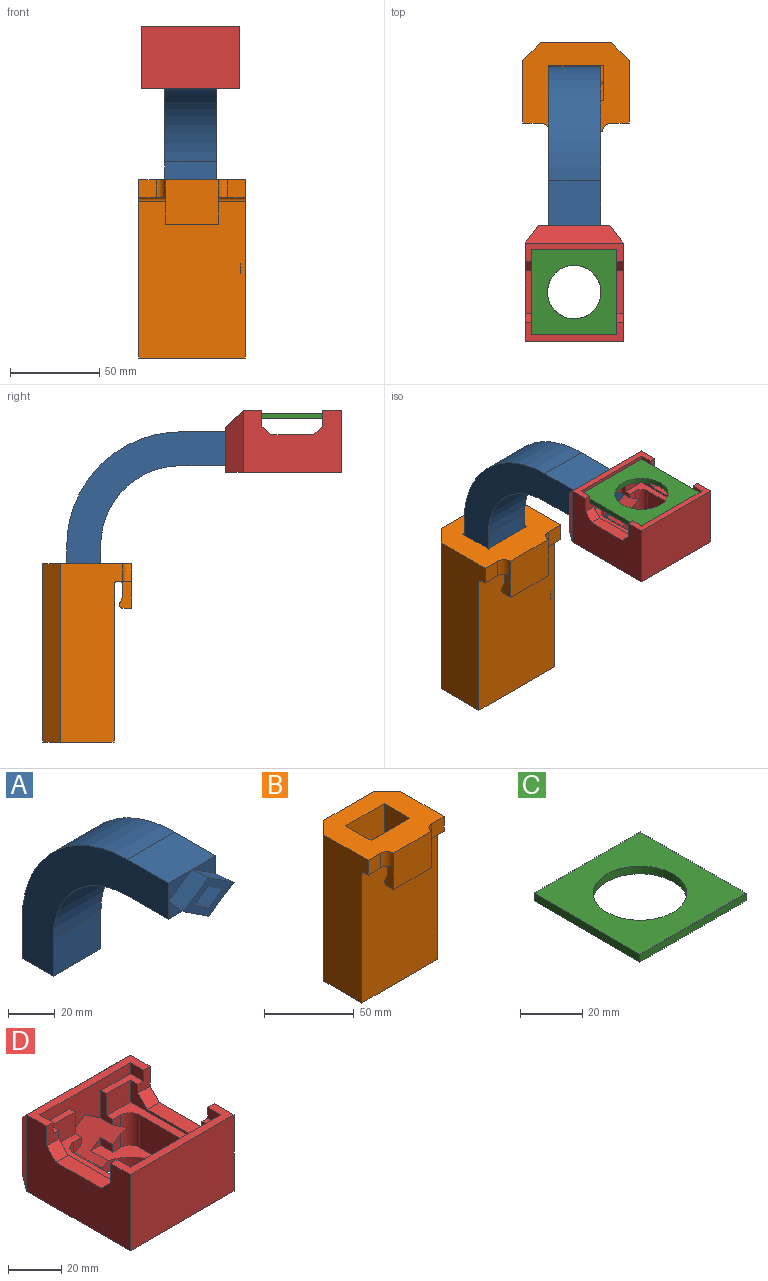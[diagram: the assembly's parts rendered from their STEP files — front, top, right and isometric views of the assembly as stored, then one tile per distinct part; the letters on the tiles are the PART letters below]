
ASSEMBLY  parts=4 mates=3
PART A: 34 faces, bbox 30.9x99x84.6 mm
  f0: plane 14.5x9.5mm, normal (0,-1,0), area 68.9mm2, adj f6,f11,f12
  f1: plane 14.5x9.5mm, normal (0,-1,0), area 68.9mm2, adj f5,f6,f19
  f2: plane 14.5x9.5mm, normal (0,-1,0), area 68.9mm2, adj f4,f5,f14
  f3: plane 14.5x9.5mm, normal (0,-1,0), area 68.9mm2, adj f4,f11,f13
  f4: plane 29x25mm, normal (0,0,-1), area 725mm2, adj f2,f3,f5,f11,f24
  f5: plane 89x84mm, normal (1,0,0), area 2481.6mm2, adj f1,f2,f4,f6,f24,f25,f30,f31
  f6: plane 29x25mm, normal (0,0,1), area 725mm2, adj f0,f1,f5,f11,f25
  f7: plane 25x9.24mm, normal (0.6,0,0.8), area 287.4mm2, adj f8,f10,f15,f22
  f8: plane 25x9.24mm, normal (0.6,0,-0.8), area 287.4mm2, adj f7,f9,f16,f21
  f9: plane 25x9.24mm, normal (-0.6,0,-0.8), area 287.4mm2, adj f8,f10,f17,f26
  f10: plane 25x9.24mm, normal (-0.6,0,0.8), area 287.4mm2, adj f7,f9,f18,f23
  f11: plane 89x84mm, normal (-1,0,0), area 2481.6mm2, adj f0,f3,f4,f6,f24,f25,f30,f31
  f12: plane 15.46x10.13mm, normal (-0.55,0.05,0.84), area 179.3mm2, adj f0,f13,f19,f20
  f13: plane 15.46x10.13mm, normal (-0.55,0.05,-0.84), area 179.3mm2, adj f3,f12,f14,f20
  f14: plane 15.46x10.13mm, normal (0.55,0.05,-0.84), area 179.3mm2, adj f2,f13,f19,f20
  f15: plane 10x9.24mm, normal (0.59,0.05,0.8), area 109.6mm2, adj f7,f16,f18,f20
  f16: plane 10x9.24mm, normal (0.59,0.05,-0.8), area 109.6mm2, adj f8,f15,f17,f20
  f17: plane 10x9.24mm, normal (-0.59,0.05,-0.8), area 109.6mm2, adj f9,f16,f18,f20
  f18: plane 10x9.24mm, normal (-0.59,0.05,0.8), area 109.6mm2, adj f10,f15,f17,f20
  f19: plane 15.46x10.13mm, normal (0.55,0.05,0.84), area 179.3mm2, adj f1,f12,f14,f20
  f20: plane 30.91x20.25mm, normal (0,-1,0), area 209.5mm2, adj f12,f13,f14,f15,f16,f17,f18,f19
  f21: cone r=61.35mm half-angle=36.6deg, axis (1,0,0), area 1046.1mm2, adj f8,f22,f26,f27
  f22: cone r=54.5mm half-angle=36.6deg, axis (-1,0,0), area 922.4mm2, adj f7,f21,f23,f28
  f23: cone r=47.65mm half-angle=36.6deg, axis (1,0,0), area 922.4mm2, adj f10,f22,f26,f29
  f24: cylinder r=45mm len=45mm, axis (1,0,0), area 2049.9mm2, adj f4,f5,f11,f30
  f25: cylinder r=64mm len=64mm, axis (1,0,0), area 2915.4mm2, adj f5,f6,f11,f31
  f26: cone r=54.5mm half-angle=36.6deg, axis (-1,0,0), area 1046.1mm2, adj f9,f21,f23,f32
  f27: plane 20x9.24mm, normal (0.6,-0.8,0), area 229.9mm2, adj f21,f28,f32,f33
  f28: plane 20x9.24mm, normal (0.6,0.8,0), area 229.9mm2, adj f22,f27,f29,f33
  f29: plane 20x9.24mm, normal (-0.6,0.8,0), area 229.9mm2, adj f23,f28,f32,f33
  f30: plane 29x20mm, normal (0,-1,0), area 580mm2, adj f5,f11,f24,f33
  f31: plane 29x20mm, normal (0,1,0), area 580mm2, adj f5,f11,f25,f33
  f32: plane 20x9.24mm, normal (-0.6,-0.8,0), area 229.9mm2, adj f26,f27,f29,f33
  f33: plane 29x19mm, normal (0,0,-1), area 424.5mm2, adj f5,f11,f27,f28,f29,f30,f31,f32
PART B: 74 faces, bbox 60x50x100 mm
  f0: plane 39.73x22.93mm, normal (-1,0,0), area 855.9mm2, adj f3,f4,f39,f41,f43,f47,f66
  f1: plane 100x35mm, normal (1,0,0), area 2326.3mm2, adj f4,f9,f15,f25,f26,f29,f32,f62
  f2: cylinder r=3.5mm len=7mm, axis (1,0,0), area 44mm2, adj f35,f63
  f3: plane 70x50mm, normal (0,1,0), area 2997.6mm2, adj f0,f4,f36,f40,f41,f42,f44,f45
  f4: plane 60x40mm, normal (0,0,-1), area 850mm2, adj f0,f1,f3,f13,f14,f15,f16,f25
  f5: plane 15.25x10mm, normal (0.55,0.84,0), area 182.4mm2, adj f6,f8,f19,f40
  f6: plane 15.25x10mm, normal (0.55,-0.84,0), area 182.4mm2, adj f5,f7,f24,f40
  f7: plane 15.25x10mm, normal (-0.55,-0.84,0), area 182.4mm2, adj f6,f8,f22,f40
  f8: plane 15.25x10mm, normal (-0.55,0.84,0), area 182.4mm2, adj f5,f7,f23,f40
  f9: plane 60x50mm, normal (0,0,1), area 2150.7mm2, adj f1,f11,f13,f14,f15,f16,f17,f18
  f10: plane 30x5mm, normal (0,0,-1), area 150mm2, adj f11,f28,f30,f54
  f11: plane 30x25mm, normal (0,-1,0), area 750mm2, adj f9,f10,f28,f30,f33,f34
  f12: plane 30x5.71mm, normal (0,1,0), area 171.3mm2, adj f28,f30,f31,f55
  f13: plane 100x35mm, normal (-1,0,0), area 3050.9mm2, adj f4,f9,f16,f25,f26,f27,f32
  f14: plane 100x40mm, normal (0,1,0), area 4000mm2, adj f4,f9,f15,f16
  f15: plane 100x10mm, normal (0.71,0.71,0), area 1407mm2, adj f1,f4,f9,f14,f62
  f16: plane 100x10mm, normal (-0.71,0.71,0), area 1414.2mm2, adj f4,f9,f13,f14
  f17: plane 20x20mm, normal (1,0,0), area 400mm2, adj f9,f18,f19,f21,f24
  f18: plane 30.5x20mm, normal (0,1,0), area 610mm2, adj f9,f17,f19,f20,f23
  f19: plane 15.25x10mm, normal (0,0,1), area 76.3mm2, adj f5,f17,f18
  f20: plane 20x20mm, normal (-1,0,0), area 400mm2, adj f9,f18,f21,f22,f23
  f21: plane 30.5x20mm, normal (0,-1,0), area 610mm2, adj f9,f17,f20,f22,f24
  f22: plane 15.25x10mm, normal (0,0,1), area 76.2mm2, adj f7,f20,f21
  f23: plane 15.25x10mm, normal (0,0,1), area 76.2mm2, adj f8,f18,f20
  f24: plane 15.25x10mm, normal (0,0,1), area 76.3mm2, adj f6,f17,f21
  f25: plane 88x60mm, normal (0,-1,0), area 5280mm2, adj f1,f4,f13,f32
  f26: plane 60x8mm, normal (0,0,-1), area 130.7mm2, adj f1,f13,f27,f28,f29,f30,f31,f32
  f27: plane 10x10mm, normal (0,-1,0), area 100mm2, adj f9,f13,f26,f33
  f28: plane 15x7mm, normal (-1,0,0), area 84.4mm2, adj f10,f11,f12,f26,f31,f54,f55
  f29: plane 10x10mm, normal (0,-1,0), area 100mm2, adj f1,f9,f26,f34
  f30: plane 15x7mm, normal (1,0,0), area 84.4mm2, adj f10,f11,f12,f26,f31,f54,f55
  f31: cylinder r=2mm len=30mm, axis (-1,0,0), area 94.2mm2, adj f12,f26,f28,f30
  f32: cylinder r=2mm len=60mm, axis (1,0,0), area 188.5mm2, adj f1,f13,f25,f26
  f33: cylinder r=5mm len=10mm, axis (0,0,1), area 78.5mm2, adj f9,f11,f26,f27
  f34: cylinder r=5mm len=10mm, axis (0,0,-1), area 78.5mm2, adj f9,f11,f26,f29
  f35: plane 29.35x21.73mm, normal (-1,0,0), area 476.4mm2, adj f2,f39,f40,f64,f67,f68,f69,f72
  f36: plane 70x22.93mm, normal (1,0,0), area 1547.2mm2, adj f3,f4,f37,f40,f44,f46,f48
  f37: plane 70x7.07mm, normal (0.71,-0.71,0), area 700mm2, adj f4,f36,f38,f40
  f38: plane 70x35.86mm, normal (0,-1,0), area 2435.1mm2, adj f4,f37,f39,f40,f49,f50,f51,f53
  f39: plane 70x7.07mm, normal (-0.71,-0.71,0), area 700mm2, adj f0,f4,f35,f38,f40,f65
  f40: plane 50x30mm, normal (0,0,-1), area 1137.8mm2, adj f3,f5,f6,f7,f8,f35,f36,f37
  f41: plane 5x5mm, normal (0,0,-1), area 21.9mm2, adj f0,f3,f42,f43,f56
  f42: plane 15x5mm, normal (-1,0,0), area 55mm2, adj f3,f41,f43,f47
  f43: plane 7x5mm, normal (0,1,0), area 35mm2, adj f0,f41,f42,f47
  f44: plane 5x5mm, normal (0,0,-1), area 21.9mm2, adj f3,f36,f45,f46,f58
  f45: plane 13.13x5mm, normal (1,0,0), area 57.8mm2, adj f3,f44,f46,f48
  f46: plane 10x5mm, normal (0,1,0), area 50mm2, adj f36,f44,f45,f48
  f47: plane 8x5mm, normal (0,0.85,0.53), area 47.2mm2, adj f0,f3,f42,f43
  f48: plane 5x5mm, normal (0,0.53,0.85), area 29.5mm2, adj f3,f36,f45,f46
  f49: plane 15x5mm, normal (-1,0,0), area 50mm2, adj f38,f50,f52,f53
  f50: plane 5x5mm, normal (0,0,-1), area 21.7mm2, adj f38,f49,f51,f52,f60
  f51: plane 15x5mm, normal (1,0,0), area 50mm2, adj f38,f50,f52,f53
  f52: plane 5x5mm, normal (0,-1,0), area 25mm2, adj f49,f50,f51,f53
  f53: plane 10x5mm, normal (0,-0.89,0.45), area 55.9mm2, adj f38,f49,f51,f52
  f54: cylinder r=2mm len=30mm, axis (-1,0,0), area 137.6mm2, adj f10,f28,f30,f55
  f55: plane 30x3.97mm, normal (0,0.94,0.35), area 127.3mm2, adj f12,f28,f30,f54
  f56: cylinder r=0.99mm len=5mm, axis (0,0,-1), area 31.1mm2, adj f41,f57
  f57: plane 1.98x1.98mm, normal (0,0,-1), area 3.1mm2, adj f56
  f58: cylinder r=0.99mm len=5mm, axis (0,0,-1), area 31mm2, adj f44,f59
  f59: plane 1.97x1.97mm, normal (0,0,-1), area 3.1mm2, adj f58
  f60: cylinder r=1.02mm len=5mm, axis (0,0,-1), area 32mm2, adj f50,f61
  f61: plane 2.04x2.04mm, normal (0,0,-1), area 3.3mm2, adj f60
  f62: cylinder r=15.24mm len=30.48mm, axis (1,0,0), area 282.1mm2, adj f1,f15,f63
  f63: plane 30.48x30.48mm, normal (1,0,0), area 691.2mm2, adj f2,f62
  f64: plane 19.98x12.7mm, normal (0,-1,0), area 173.8mm2, adj f35,f69,f70,f72,f73
  f65: plane 30.26x12.7mm, normal (0,1,0), area 304.3mm2, adj f39,f66,f70,f72,f73
  f66: plane 22.93x12.7mm, normal (0,0,-1), area 291.2mm2, adj f0,f3,f65,f70
  f67: plane 20x12.7mm, normal (0,1,0), area 231.4mm2, adj f35,f40,f68,f70,f71
  f68: cylinder r=9.35mm len=18.7mm, axis (1,0,0), area 373mm2, adj f35,f67,f69,f70
  f69: plane 12.7x0.18mm, normal (0,0,1), area 2.2mm2, adj f35,f64,f68,f70
  f70: plane 23.54x22.93mm, normal (-1,0,0), area 130.4mm2, adj f3,f64,f65,f66,f67,f68,f69,f71
  f71: plane 6.73x6.73mm, normal (-0.71,0,0.71), area 11.4mm2, adj f3,f40,f67,f70
  f72: plane 9.7x9.7mm, normal (-0.71,0,0.71), area 39.1mm2, adj f35,f64,f65,f73
  f73: cylinder r=5mm len=4.58mm, axis (0,-1,0), area 16.5mm2, adj f64,f65,f70,f72
PART C: 7 faces, bbox 48x48x3 mm
  f0: plane 48x3mm, normal (0,1,0), area 144mm2, adj f1,f3,f4,f5
  f1: plane 48x3mm, normal (-1,0,0), area 144mm2, adj f0,f2,f4,f5
  f2: plane 48x3mm, normal (0,-1,0), area 144mm2, adj f1,f3,f4,f5
  f3: plane 48x3mm, normal (1,0,0), area 144mm2, adj f0,f2,f4,f5
  f4: plane 48x48mm, normal (0,0,1), area 1597.1mm2, adj f0,f1,f2,f3,f6
  f5: plane 48x48mm, normal (0,0,-1), area 1597.1mm2, adj f0,f1,f2,f3,f6
  f6: cylinder r=15mm len=30mm, axis (0,0,1), area 282.7mm2, adj f4,f5
PART D: 58 faces, bbox 55x65x35 mm
  f0: plane 15.72x7mm, normal (0,0,1), area 59.2mm2, adj f4,f6,f30,f32,f43,f51
  f1: plane 15.72x7mm, normal (0,0,1), area 59.2mm2, adj f3,f5,f16,f32,f42,f48
  f2: plane 55x35mm, normal (1,0,0), area 1474mm2, adj f7,f18,f22,f25,f36,f48,f49,f50
  f3: plane 42x10mm, normal (-1,0,0), area 139mm2, adj f1,f15,f16,f17,f31,f48,f49,f50
  f4: plane 42x10mm, normal (1,0,0), area 139mm2, adj f0,f15,f17,f30,f31,f51,f52,f53
  f5: plane 7x5mm, normal (-1,0,0), area 35mm2, adj f1,f7,f32,f48
  f6: plane 7x5mm, normal (1,0,0), area 35mm2, adj f0,f7,f32,f51
  f7: plane 55x10.5mm, normal (0,0,1), area 241.5mm2, adj f2,f5,f6,f21,f32,f41,f48,f51
  f8: plane 6.33x4.22mm, normal (0,-1,0), area 20.8mm2, adj f12,f24,f38,f44
  f9: plane 6.33x4.22mm, normal (0,-1,0), area 20.8mm2, adj f13,f24,f37,f46
  f10: plane 5.28x3.52mm, normal (0,-1,0), area 9.3mm2, adj f12,f24,f44
  f11: plane 5.28x3.52mm, normal (0,-1,0), area 9.3mm2, adj f13,f24,f46
  f12: plane 6.5x3.52mm, normal (-1,0,0), area 22.9mm2, adj f8,f10,f24,f44
  f13: plane 6.5x3.52mm, normal (1,0,0), area 22.9mm2, adj f9,f11,f24,f46
  f14: plane 5.33x4.22mm, normal (0,-1,0), area 16.6mm2, adj f15,f38,f42,f45
  f15: plane 42x42mm, normal (0,0,1), area 502.5mm2, adj f3,f4,f14,f16,f26,f27,f28,f29
  f16: plane 12.72x10mm, normal (0,-1,0), area 127.2mm2, adj f1,f3,f15,f42
  f17: plane 48x7mm, normal (0,0,1), area 168mm2, adj f3,f4,f31,f33,f34,f35,f49,f53
  f18: plane 35x10mm, normal (0.8,0.6,0), area 375mm2, adj f2,f19,f25,f41
  f19: plane 40x25mm, normal (0,1,0), area 700mm2, adj f18,f20,f25,f41,f44,f45,f46,f47
  f20: plane 35x10mm, normal (-0.8,0.6,0), area 375mm2, adj f19,f21,f25,f41
  f21: plane 55x35mm, normal (-1,0,0), area 1474mm2, adj f7,f20,f22,f25,f36,f51,f52,f53
  f22: plane 55x35mm, normal (0,-1,0), area 1925mm2, adj f2,f21,f25,f36
  f23: cylinder r=15mm len=30mm, axis (0,0,-1), area 465.2mm2, adj f24,f25,f44,f46
  f24: plane 41.5x35mm, normal (0,0,1), area 549.7mm2, adj f8,f9,f10,f11,f12,f13,f23,f26
  f25: plane 65x55mm, normal (0,0,-1), area 2793.1mm2, adj f2,f18,f19,f20,f21,f22,f23
  f26: plane 25x15mm, normal (1,0,0), area 375mm2, adj f15,f24,f37,f40
  f27: plane 5.33x4.22mm, normal (0,-1,0), area 16.6mm2, adj f15,f37,f43,f47
  f28: plane 25x15mm, normal (-1,0,0), area 375mm2, adj f15,f24,f38,f39
  f29: plane 25x15mm, normal (0,1,0), area 375mm2, adj f15,f24,f39,f40
  f30: plane 12.72x10mm, normal (0,-1,0), area 127.2mm2, adj f0,f4,f15,f43
  f31: plane 42x10mm, normal (0,1,0), area 420mm2, adj f3,f4,f15,f17
  f32: plane 48x17.52mm, normal (0,-1,0), area 401.7mm2, adj f0,f1,f5,f6,f7,f42,f43,f45
  f33: plane 7x5mm, normal (-1,0,0), area 35mm2, adj f17,f34,f36,f49
  f34: plane 48x5mm, normal (0,1,0), area 240mm2, adj f17,f33,f35,f36
  f35: plane 7x5mm, normal (1,0,0), area 35mm2, adj f17,f34,f36,f53
  f36: plane 55x10.5mm, normal (0,0,1), area 241.5mm2, adj f2,f21,f22,f33,f34,f35,f49,f53
  f37: cylinder r=5mm len=15mm, axis (0,0,-1), area 113.5mm2, adj f9,f15,f24,f26,f27,f46,f47
  f38: cylinder r=5mm len=15mm, axis (0,0,1), area 113.5mm2, adj f8,f14,f15,f24,f28,f44,f45
  f39: cylinder r=5mm len=15mm, axis (0,0,-1), area 117.8mm2, adj f15,f24,f28,f29
  f40: cylinder r=5mm len=15mm, axis (0,0,1), area 117.8mm2, adj f15,f24,f26,f29
  f41: plane 55x10mm, normal (0,0.71,0.71), area 671.8mm2, adj f7,f18,f19,f20
  f42: plane 12.52x6.5mm, normal (-1,0,0), area 46.4mm2, adj f1,f14,f15,f16,f32,f45
  f43: plane 12.52x6.5mm, normal (1,0,0), area 46.4mm2, adj f0,f15,f27,f30,f32,f47
  f44: plane 22.81x15.01mm, normal (-0.55,0,0.83), area 329.3mm2, adj f8,f10,f12,f19,f23,f24,f38,f45
  f45: plane 20.67x15mm, normal (-0.55,0,-0.83), area 296.5mm2, adj f14,f19,f32,f38,f42,f44,f47
  f46: plane 22.81x15.01mm, normal (0.55,0,0.83), area 329.3mm2, adj f9,f11,f13,f19,f23,f24,f37,f44
  f47: plane 20.67x15mm, normal (0.55,0,-0.83), area 296.5mm2, adj f19,f27,f32,f37,f43,f45,f46
  f48: plane 9x6.5mm, normal (0,-1,0), area 43.5mm2, adj f1,f2,f3,f5,f7,f55
  f49: plane 9x6.5mm, normal (0,1,0), area 43.5mm2, adj f2,f3,f17,f33,f36,f56
  f50: plane 24x6.5mm, normal (0,0,1), area 156mm2, adj f2,f3,f55,f56
  f51: plane 9x6.5mm, normal (0,-1,0), area 43.5mm2, adj f0,f4,f6,f7,f21,f54
  f52: plane 24x6.5mm, normal (0,0,1), area 156mm2, adj f4,f21,f54,f57
  f53: plane 9x6.5mm, normal (0,1,0), area 43.5mm2, adj f4,f17,f21,f35,f36,f57
  f54: plane 6.5x5mm, normal (0,-0.71,0.71), area 46mm2, adj f4,f21,f51,f52
  f55: plane 6.5x5mm, normal (0,-0.71,0.71), area 46mm2, adj f2,f3,f48,f50
  f56: plane 6.5x5mm, normal (0,0.71,0.71), area 46mm2, adj f2,f3,f49,f50
  f57: plane 6.5x5mm, normal (0,0.71,0.71), area 46mm2, adj f4,f21,f52,f53
PLACE A t=(4.02,36.99,13.89)mm
PLACE B t=(4.77,116.99,-50.61)mm
PLACE C t=(3.77,-0.51,0.64)mm
PLACE D t=(3.77,-0.51,0.64)mm
MATE fastened D.f0 <-> C.f5  axis (0,0,1) through (-20.23,23.49,30.64)mm
MATE fastened A.f1 <-> D.f19  axis (0,-1,0) through (11.27,36.99,18.64)mm
MATE fastened A.f11 <-> B.f17  axis (-1,0,0) through (-10.48,106.99,-50.61)mm
